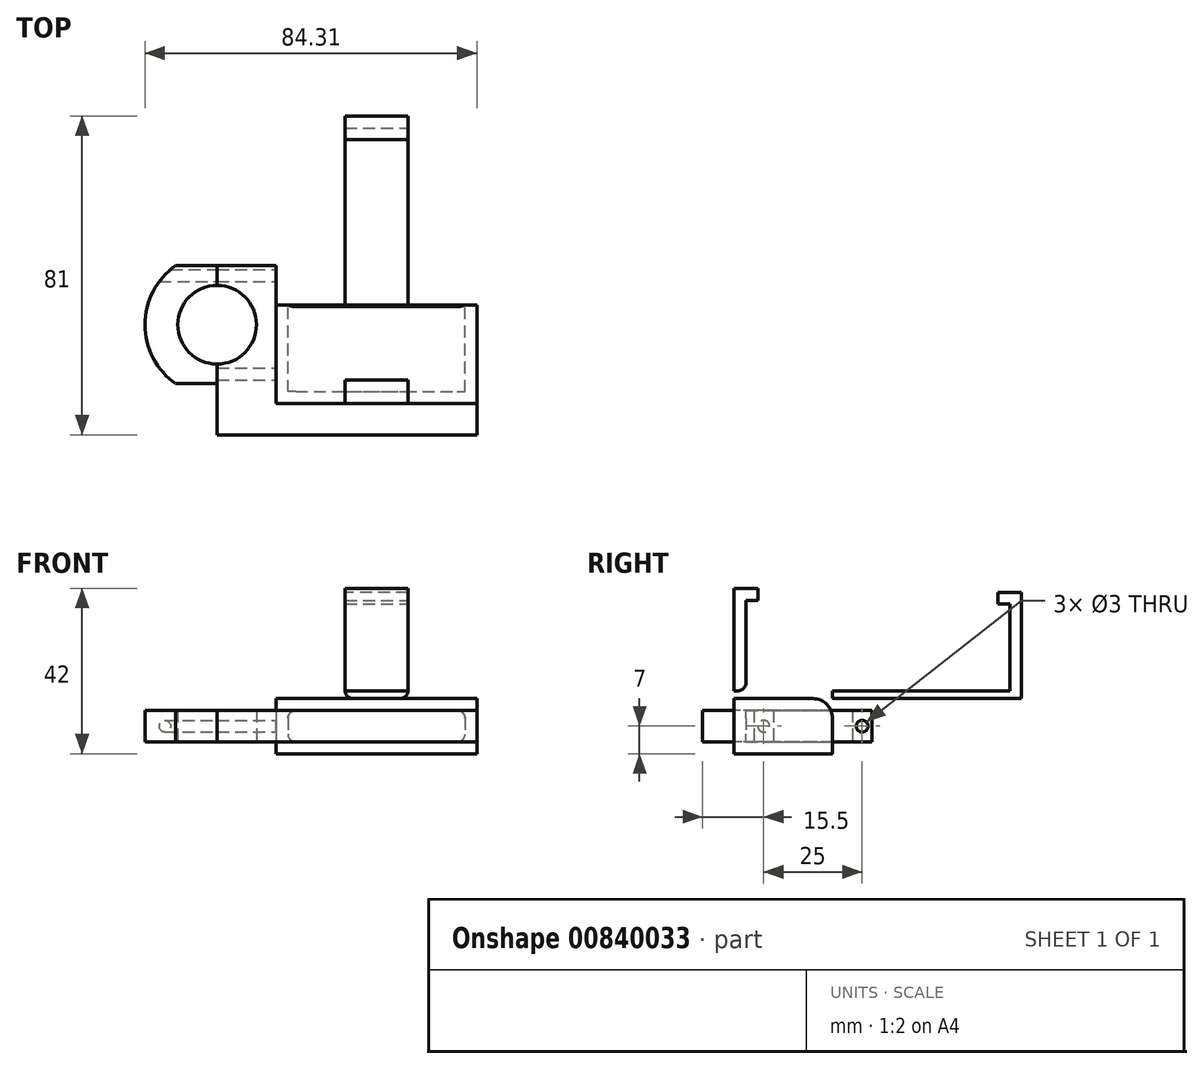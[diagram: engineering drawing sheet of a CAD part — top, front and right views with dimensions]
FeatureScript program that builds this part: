
annotation { "Feature Type Name" : "Feature", "Feature Type Description" : "" }
export const myFeature = defineFeature(function(context is Context, id is Id, definition is map)
    precondition{}
    {
        {
            var Q0;
            Q0=qCreatedBy(makeId("Top.planeOp"),FACE);
            var sketch = newSketch(context, id + "F0", { "sketchPlane" : qUnion([Q0])});
            skArc(sketch, "E0", {"start": v(0, 10) * mm, "mid": v(-10, 0) * mm, "end": v(0, -10) * mm});
            skLineSegment(sketch, "E1.bottom", {"start": v(0, 10) * mm, "end": v(-10.5, 10) * mm});
            skLineSegment(sketch, "E1.top", {"start": v(0, 15) * mm, "end": v(-10.5, 15) * mm});
            skLineSegment(sketch, "E1.left", {"start": v(0, 10) * mm, "end": v(0, 15) * mm});
            skLineSegment(sketch, "E1.right", {"start": v(-10.5, 10) * mm, "end": v(-10.5, 15) * mm});
            skLineSegment(sketch, "E2.MirrorCS", {"start": v(0, -10) * mm, "end": v(-10.5, -10) * mm});
            skLineSegment(sketch, "E3.MirrorCS", {"start": v(-10.5, -10) * mm, "end": v(-10.5, -15) * mm});
            skLineSegment(sketch, "E4.MirrorCS", {"start": v(0, -15) * mm, "end": v(-10.5, -15) * mm});
            skLineSegment(sketch, "E5.MirrorCS", {"start": v(0, -10) * mm, "end": v(0, -15) * mm});
            skArc(sketch, "E6", {"start": v(-10.5, 15) * mm, "mid": v(-18.3, 0) * mm, "end": v(-10.5, -15) * mm});
            skSolve(sketch);
        }
        {
            var Q0;
            Q0=makeQuery(id+"F0.imprint","IMPRINT",FACE,{"disambiguationData":[TD([[makeQuery(id+"F0.imprint","IMPRINT",EDGE,{"derivedFrom":sQuery(id+"F0.wireOp",EDGE,"E1.bottom")}),-1.0]])]});
            var Q1;
            Q1=makeQuery(id+"F0.imprint","IMPRINT",FACE,{"disambiguationData":[TD([[makeQuery(id+"F0.imprint","IMPRINT",EDGE,{"derivedFrom":sQuery(id+"F0.wireOp",EDGE,"E0")}),-1.0]])]});
            var Q2;
            Q2=makeQuery(id+"F0.imprint","IMPRINT",FACE,{"disambiguationData":[TD([[makeQuery(id+"F0.imprint","IMPRINT",EDGE,{"derivedFrom":sQuery(id+"F0.wireOp",EDGE,"E2.MirrorCS")}),1.0]])]});
            extrude(context, id + "F1", {"entities" : qUnion([Q0, Q1, Q2]), "depth" : 8 * mm, "offsetDistance" : 25 * mm});
        }
        {
            var Q0;
            Q0=makeQuery(id+"F1.opExtrude","SWEPT_FACE",FACE,{"disambiguationData":[OSD([sQuery(id+"F0.wireOp",EDGE,"E1.left")])]});
            var sketch = newSketch(context, id + "F2", { "sketchPlane" : qUnion([Q0])});
            skCircle(sketch, "E7", {"center": v(12.5, 4) * mm, "radius": 1.5 * mm});
            skPoint(sketch, "E7.centerSnap0", {"position": v(10, 4) * mm});
            skPoint(sketch, "E7.centerSnap1", {"position": v(12.5, 8) * mm});
            skCircle(sketch, "E8.MirrorC", {"center": v(-12.5, 4) * mm, "radius": 1.5 * mm});
            skSolve(sketch);
        }
        {
            var Q0;
            Q0=makeQuery(id+"F2.imprint","IMPRINT",FACE,{"disambiguationData":[TD([[makeQuery(id+"F2.imprint","IMPRINT",EDGE,{"derivedFrom":sQuery(id+"F2.wireOp",EDGE,"E7")}),1.0]])]});
            var Q1;
            Q1=makeQuery(id+"F2.imprint","IMPRINT",FACE,{"disambiguationData":[TD([[makeQuery(id+"F2.imprint","IMPRINT",EDGE,{"derivedFrom":sQuery(id+"F2.wireOp",EDGE,"E8.MirrorC")}),-1.0]])]});
            extrude(context, id + "F3", {"entities" : qUnion([Q0, Q1]), "operationType" : NewBodyOperationType.REMOVE, "endBound" : BoundingType.UP_TO_NEXT, "oppositeDirection" : true, "depth" : 25 * mm, "offsetDistance" : 25 * mm});
        }
        {
            var Q0;
            Q0=qCreatedBy(makeId("Top.planeOp"),FACE);
            var sketch = newSketch(context, id + "F4", { "sketchPlane" : qUnion([Q0])});
            skLineSegment(sketch, "E9.0", {"start": v(0, 15) * mm, "end": v(-10.5, 15) * mm});
            skLineSegment(sketch, "E9.1", {"start": v(0, 10) * mm, "end": v(0, 15) * mm});
            skArc(sketch, "E9.2", {"start": v(0, 10) * mm, "mid": v(-10, 0) * mm, "end": v(0, -10) * mm});
            skLineSegment(sketch, "E9.3", {"start": v(0, -10) * mm, "end": v(0, -15) * mm});
            skLineSegment(sketch, "E9.4", {"start": v(0, -15) * mm, "end": v(-10.5, -15) * mm});
            skArc(sketch, "E9.5", {"start": v(-10.5, 15) * mm, "mid": v(-18.3, 0) * mm, "end": v(-10.5, -15) * mm});
            skArc(sketch, "E10", {"start": v(0, -10) * mm, "mid": v(10, 0) * mm, "end": v(0, 10) * mm});
            skLineSegment(sketch, "E11.bottom", {"start": v(0, 10) * mm, "end": v(15, 10) * mm});
            skLineSegment(sketch, "E11.top", {"start": v(0, 15) * mm, "end": v(15, 15) * mm});
            skLineSegment(sketch, "E11.right", {"start": v(15, 10) * mm, "end": v(15, 15) * mm});
            skLineSegment(sketch, "E12.MirrorCS", {"start": v(0, -10) * mm, "end": v(15, -10) * mm});
            skLineSegment(sketch, "E13.MirrorCS", {"start": v(15, -10) * mm, "end": v(15, -15) * mm});
            skLineSegment(sketch, "E14.MirrorCS", {"start": v(0, -15) * mm, "end": v(15, -15) * mm});
            skLineSegment(sketch, "E15", {"start": v(15, 10) * mm, "end": v(15, -10) * mm});
            skLineSegment(sketch, "E16.top", {"start": v(0, -20) * mm, "end": v(15, -20) * mm});
            skLineSegment(sketch, "E16.left", {"start": v(0, -15) * mm, "end": v(0, -20) * mm});
            skLineSegment(sketch, "E16.right", {"start": v(15, -15) * mm, "end": v(15, -20) * mm});
            skLineSegment(sketch, "E17.bottom", {"start": v(0, -20) * mm, "end": v(66, -20) * mm});
            skLineSegment(sketch, "E17.top", {"start": v(0, -28) * mm, "end": v(66, -28) * mm});
            skLineSegment(sketch, "E17.left", {"start": v(0, -20) * mm, "end": v(0, -28) * mm});
            skLineSegment(sketch, "E17.right", {"start": v(66, -20) * mm, "end": v(66, -28) * mm});
            skSolve(sketch);
        }
        {
            var Q0;
            Q0=makeQuery(id+"F4.imprint","IMPRINT",FACE,{"disambiguationData":[TD([[makeQuery(id+"F4.imprint","IMPRINT",EDGE,{"derivedFrom":sQuery(id+"F4.wireOp",EDGE,"E10")}),-1.0]])]});
            var Q1;
            Q1=makeQuery(id+"F4.imprint","IMPRINT",FACE,{"disambiguationData":[TD([[makeQuery(id+"F4.imprint","IMPRINT",EDGE,{"derivedFrom":sQuery(id+"F4.wireOp",EDGE,"E9.1")}),-1.0]])]});
            var Q2;
            Q2=makeQuery(id+"F4.imprint","IMPRINT",FACE,{"disambiguationData":[TD([[makeQuery(id+"F4.imprint","IMPRINT",EDGE,{"derivedFrom":sQuery(id+"F4.wireOp",EDGE,"E9.3")}),1.0]])]});
            var Q3;
            Q3=makeQuery(id+"F4.imprint","IMPRINT",FACE,{"disambiguationData":[TD([[makeQuery(id+"F4.imprint","IMPRINT",EDGE,{"derivedFrom":sQuery(id+"F4.wireOp",EDGE,"QlJfyb3Y-pkJ5-ScCR-3cII-RCXO0TggYRWT.top")}),1.0]])]});
            var Q4;
            Q4=makeQuery(id+"F4.imprint","IMPRINT",FACE,{"disambiguationData":[TD([[makeQuery(id+"F4.imprint","IMPRINT",EDGE,{"derivedFrom":sQuery(id+"F4.wireOp",EDGE,"E14.MirrorCS")}),-1.0]])]});
            var Q5;
            Q5=makeQuery(id+"F4.imprint","IMPRINT",FACE,{"disambiguationData":[TD([[makeQuery(id+"F4.imprint","IMPRINT",EDGE,{"derivedFrom":sQuery(id+"F4.wireOp",EDGE,"E16.top")}),-1.0]])]});
            extrude(context, id + "F5", {"entities" : qUnion([Q0, Q1, Q2, Q3, Q4, Q5]), "depth" : 8 * mm, "offsetDistance" : 25 * mm});
        }
        {
            var Q0;
            Q0=makeQuery(id+"F5.opExtrude","SWEPT_FACE",FACE,{"disambiguationData":[OSD([sQuery(id+"F4.wireOp",EDGE,"E11.right"),sQuery(id+"F4.wireOp",EDGE,"E13.MirrorCS"),sQuery(id+"F4.wireOp",EDGE,"E15"),sQuery(id+"F4.wireOp",EDGE,"E16.right")])]});
            var sketch = newSketch(context, id + "F6", { "sketchPlane" : qUnion([Q0])});
            skCircle(sketch, "E18.0", {"center": v(12.5, 4) * mm, "radius": 1.5 * mm});
            skCircle(sketch, "E18.1", {"center": v(-12.5, 4) * mm, "radius": 1.5 * mm});
            skSolve(sketch);
        }
        {
            var Q0;
            Q0=makeQuery(id+"F6.imprint","IMPRINT",FACE,{"disambiguationData":[TD([[makeQuery(id+"F6.imprint","IMPRINT",EDGE,{"derivedFrom":sQuery(id+"F6.wireOp",EDGE,"E18.1")}),1.0]])]});
            var Q1;
            Q1=makeQuery(id+"F6.imprint","IMPRINT",FACE,{"disambiguationData":[TD([[makeQuery(id+"F6.imprint","IMPRINT",EDGE,{"derivedFrom":sQuery(id+"F6.wireOp",EDGE,"E18.0")}),1.0]])]});
            extrude(context, id + "F7", {"entities" : qUnion([Q0, Q1]), "operationType" : NewBodyOperationType.REMOVE, "endBound" : BoundingType.UP_TO_NEXT, "oppositeDirection" : true, "depth" : 25 * mm, "offsetDistance" : 25 * mm});
        }
        {
            var Q0;
            Q0=makeQuery(id+"F5.opExtrude","SWEPT_FACE",FACE,{"disambiguationData":[OSD([sQuery(id+"F4.wireOp",EDGE,"E17.bottom")])]});
            var sketch = newSketch(context, id + "F8", { "sketchPlane" : qUnion([Q0])});
            skLineSegment(sketch, "E19.bottom", {"start": v(-15, 11) * mm, "end": v(-66, 11) * mm});
            skLineSegment(sketch, "E19.top", {"start": v(-15, -3) * mm, "end": v(-66, -3) * mm});
            skLineSegment(sketch, "E19.left", {"start": v(-15, 11) * mm, "end": v(-15, -3) * mm});
            skLineSegment(sketch, "E19.right", {"start": v(-66, 11) * mm, "end": v(-66, -3) * mm});
            skSolve(sketch);
        }
        {
            var Q0;
            {var subQ0=sQuery(id+"F8.wireOp",EDGE,"E19.bottom");Q0=makeQuery(id+"F8.imprint","IMPRINT",FACE,{"disambiguationData":[TD([[makeQuery(id+"F8.imprint","IMPRINT",EDGE,{"derivedFrom":subQ0}),1.0]])]});}
            var Q1;
            {var subQ1=sQuery(id+"F4.wireOp",EDGE,"E17.bottom");var subQ2=makeQuery(id+"F5.opExtrude","CAP_EDGE",EDGE,{"disambiguationData":[OSD([subQ1])],"isStart":true});Q1=makeQuery(id+"F8.imprint","IMPRINT",FACE,{"disambiguationData":[TD([[makeQuery(id+"F8.imprint","IMPRINT",EDGE,{"derivedFrom":subQ2}),-1.0]])]});}
            var Q2;
            {var subQ0=sQuery(id+"F8.wireOp",EDGE,"E19.top");Q2=makeQuery(id+"F8.imprint","IMPRINT",FACE,{"disambiguationData":[TD([[makeQuery(id+"F8.imprint","IMPRINT",EDGE,{"derivedFrom":subQ0}),-1.0]])]});}
            extrude(context, id + "F9", {"entities" : qUnion([Q0, Q1, Q2]), "depth" : 25 * mm, "offsetDistance" : 25 * mm});
        }
        {
            var Q0;
            Q0=makeQuery(id+"F9.opExtrude","CAP_FACE",FACE,{"disambiguationData":[OSD([sQuery(id+"F8.wireOp",EDGE,"E19.bottom"),sQuery(id+"F8.wireOp",EDGE,"E19.top"),sQuery(id+"F8.wireOp",EDGE,"E19.left"),sQuery(id+"F8.wireOp",EDGE,"E19.right")])],"isStart":false});
            var sketch = newSketch(context, id + "F10", { "sketchPlane" : qUnion([Q0])});
            skLineSegment(sketch, "E20.0", {"start": v(-18, 6) * mm, "end": v(-18, 2) * mm});
            skLineSegment(sketch, "E20.1", {"start": v(-20, 8) * mm, "end": v(-61, 8) * mm});
            skLineSegment(sketch, "E20.2", {"start": v(-63, 6) * mm, "end": v(-63, 2) * mm});
            skLineSegment(sketch, "E20.3", {"start": v(-20, 0) * mm, "end": v(-61, 0) * mm});
            skPoint(sketch, "E21.visualSharp", {"position": v(-18, 8) * mm});
            skArc(sketch, "E21.filletArc", {"start": v(-18, 6) * mm, "mid": v(-18.59, 7.41) * mm, "end": v(-20, 8) * mm});
            skPoint(sketch, "E22.visualSharp", {"position": v(-18, 0) * mm});
            skArc(sketch, "E22.filletArc", {"start": v(-20, 0) * mm, "mid": v(-18.59, 0.59) * mm, "end": v(-18, 2) * mm});
            skPoint(sketch, "E23.visualSharp", {"position": v(-63, 0) * mm});
            skArc(sketch, "E23.filletArc", {"start": v(-63, 2) * mm, "mid": v(-62.41, 0.59) * mm, "end": v(-61, 0) * mm});
            skPoint(sketch, "E24.visualSharp", {"position": v(-63, 8) * mm});
            skArc(sketch, "E24.filletArc", {"start": v(-61, 8) * mm, "mid": v(-62.41, 7.41) * mm, "end": v(-63, 6) * mm});
            skSolve(sketch);
        }
        {
            var Q0;
            Q0=makeQuery(id+"F10.imprint","IMPRINT",FACE,{"disambiguationData":[TD([[makeQuery(id+"F10.imprint","IMPRINT",EDGE,{"derivedFrom":sQuery(id+"F10.wireOp",EDGE,"E20.0")}),-1.0]])]});
            extrude(context, id + "F11", {"entities" : qUnion([Q0]), "operationType" : NewBodyOperationType.REMOVE, "oppositeDirection" : true, "depth" : 22 * mm, "offsetDistance" : 25 * mm});
        }
        {
            var Q0;
            Q0=makeQuery(id+"F9.opExtrude","SWEPT_FACE",FACE,{"disambiguationData":[OSD([sQuery(id+"F8.wireOp",EDGE,"E19.bottom")])]});
            var sketch = newSketch(context, id + "F12", { "sketchPlane" : qUnion([Q0])});
            skLineSegment(sketch, "E25.0", {"start": v(66, 5) * mm, "end": v(66, -20) * mm});
            skLineSegment(sketch, "E25.1", {"start": v(15, 5) * mm, "end": v(66, 5) * mm});
            skLineSegment(sketch, "E25.2", {"start": v(15, -20) * mm, "end": v(66, -20) * mm});
            skLineSegment(sketch, "E25.3", {"start": v(15, 5) * mm, "end": v(15, -20) * mm});
            skLineSegment(sketch, "E26.bottom", {"start": v(48.5, -20) * mm, "end": v(32.5, -20) * mm});
            skLineSegment(sketch, "E26.top", {"start": v(48.5, 53) * mm, "end": v(32.5, 53) * mm});
            skLineSegment(sketch, "E26.left", {"start": v(48.5, -20) * mm, "end": v(48.5, 53) * mm});
            skLineSegment(sketch, "E26.right", {"start": v(32.5, -20) * mm, "end": v(32.5, 53) * mm});
            skPoint(sketch, "E27", {"position": v(40.5, -20) * mm});
            skSolve(sketch);
        }
        {
            var Q0;
            {var subQ5=sQuery(id+"F12.wireOp",EDGE,"E26.top");Q0=makeQuery(id+"F12.imprint","IMPRINT",FACE,{"disambiguationData":[TD([[makeQuery(id+"F12.imprint","IMPRINT",EDGE,{"derivedFrom":subQ5}),1.0]])]});}
            var Q1;
            {var subQ5=sQuery(id+"F12.wireOp",EDGE,"E26.bottom");Q1=makeQuery(id+"F12.imprint","IMPRINT",FACE,{"disambiguationData":[TD([[makeQuery(id+"F12.imprint","IMPRINT",EDGE,{"derivedFrom":subQ5}),1.0]])]});}
            extrude(context, id + "F13", {"entities" : qUnion([Q0, Q1]), "operationType" : NewBodyOperationType.ADD, "depth" : 2 * mm, "offsetDistance" : 25 * mm});
        }
        {
            var Q0;
            Q0=makeQuery(id+"F13.opExtrude","CAP_FACE",FACE,{"disambiguationData":[OSD([sQuery(id+"F12.wireOp",EDGE,"E26.bottom"),sQuery(id+"F12.wireOp",EDGE,"E26.top"),sQuery(id+"F12.wireOp",EDGE,"E26.left"),sQuery(id+"F12.wireOp",EDGE,"E26.right")])],"isStart":false});
            var sketch = newSketch(context, id + "F14", { "sketchPlane" : qUnion([Q0])});
            skLineSegment(sketch, "E28.bottom", {"start": v(48.5, -20) * mm, "end": v(32.5, -20) * mm});
            skLineSegment(sketch, "E28.top", {"start": v(48.5, -17) * mm, "end": v(32.5, -17) * mm});
            skLineSegment(sketch, "E28.left", {"start": v(48.5, -20) * mm, "end": v(48.5, -17) * mm});
            skLineSegment(sketch, "E28.right", {"start": v(32.5, -20) * mm, "end": v(32.5, -17) * mm});
            skLineSegment(sketch, "E29.bottom", {"start": v(32.5, 53) * mm, "end": v(48.5, 53) * mm});
            skLineSegment(sketch, "E29.top", {"start": v(32.5, 50) * mm, "end": v(48.5, 50) * mm});
            skLineSegment(sketch, "E29.left", {"start": v(32.5, 53) * mm, "end": v(32.5, 50) * mm});
            skLineSegment(sketch, "E29.right", {"start": v(48.5, 53) * mm, "end": v(48.5, 50) * mm});
            skSolve(sketch);
        }
        {
            var Q0;
            Q0=makeQuery(id+"F14.imprint","IMPRINT",FACE,{"disambiguationData":[TD([[makeQuery(id+"F14.imprint","IMPRINT",EDGE,{"derivedFrom":sQuery(id+"F14.wireOp",EDGE,"E29.bottom")}),1.0]])]});
            extrude(context, id + "F15", {"entities" : qUnion([Q0]), "operationType" : NewBodyOperationType.ADD, "depth" : 22 * mm, "offsetDistance" : 25 * mm});
        }
        {
            var Q0;
            Q0=makeQuery(id+"F15.opExtrude","CAP_FACE",FACE,{"disambiguationData":[OSD([sQuery(id+"F14.wireOp",EDGE,"E29.bottom"),sQuery(id+"F14.wireOp",EDGE,"E29.top"),sQuery(id+"F14.wireOp",EDGE,"E29.left"),sQuery(id+"F14.wireOp",EDGE,"E29.right")])],"isStart":false});
            var sketch = newSketch(context, id + "F16", { "sketchPlane" : qUnion([Q0])});
            skLineSegment(sketch, "E30.bottom", {"start": v(32.5, 53) * mm, "end": v(48.5, 53) * mm});
            skLineSegment(sketch, "E30.top", {"start": v(32.5, 47) * mm, "end": v(48.5, 47) * mm});
            skLineSegment(sketch, "E30.left", {"start": v(32.5, 53) * mm, "end": v(32.5, 47) * mm});
            skLineSegment(sketch, "E30.right", {"start": v(48.5, 53) * mm, "end": v(48.5, 47) * mm});
            skSolve(sketch);
        }
        {
            var Q0;
            {var subQ0=sQuery(id+"F16.wireOp",EDGE,"E30.top");Q0=makeQuery(id+"F16.imprint","IMPRINT",FACE,{"disambiguationData":[TD([[makeQuery(id+"F16.imprint","IMPRINT",EDGE,{"derivedFrom":subQ0}),1.0]])]});}
            var Q1;
            {var subQ0=sQuery(id+"F16.wireOp",EDGE,"E30.bottom");Q1=makeQuery(id+"F16.imprint","IMPRINT",FACE,{"disambiguationData":[TD([[makeQuery(id+"F16.imprint","IMPRINT",EDGE,{"derivedFrom":subQ0}),1.0]])]});}
            extrude(context, id + "F17", {"entities" : qUnion([Q0, Q1]), "operationType" : NewBodyOperationType.ADD, "depth" : 3 * mm, "offsetDistance" : 25 * mm});
        }
        {
            var Q0;
            Q0=makeQuery(id+"F13.opExtrude","CAP_FACE",FACE,{"disambiguationData":[OSD([sQuery(id+"F12.wireOp",EDGE,"E26.bottom"),sQuery(id+"F12.wireOp",EDGE,"E26.top"),sQuery(id+"F12.wireOp",EDGE,"E26.left"),sQuery(id+"F12.wireOp",EDGE,"E26.right")])],"isStart":false});
            var sketch = newSketch(context, id + "F18", { "sketchPlane" : qUnion([Q0])});
            skLineSegment(sketch, "E31.bottom", {"start": v(32.5, -20) * mm, "end": v(48.5, -20) * mm});
            skLineSegment(sketch, "E31.top", {"start": v(32.5, -17) * mm, "end": v(48.5, -17) * mm});
            skLineSegment(sketch, "E31.left", {"start": v(32.5, -20) * mm, "end": v(32.5, -17) * mm});
            skLineSegment(sketch, "E31.right", {"start": v(48.5, -20) * mm, "end": v(48.5, -17) * mm});
            skSolve(sketch);
        }
        {
            var Q0;
            Q0=makeQuery(id+"F18.imprint","IMPRINT",FACE,{"disambiguationData":[TD([[makeQuery(id+"F18.imprint","IMPRINT",EDGE,{"derivedFrom":sQuery(id+"F18.wireOp",EDGE,"E31.bottom")}),1.0]])]});
            extrude(context, id + "F19", {"entities" : qUnion([Q0]), "operationType" : NewBodyOperationType.ADD, "depth" : 23 * mm, "offsetDistance" : 25 * mm});
        }
        {
            var Q0;
            Q0=makeQuery(id+"F19.opExtrude","CAP_FACE",FACE,{"disambiguationData":[OSD([sQuery(id+"F18.wireOp",EDGE,"E31.bottom"),sQuery(id+"F18.wireOp",EDGE,"E31.top"),sQuery(id+"F18.wireOp",EDGE,"E31.left"),sQuery(id+"F18.wireOp",EDGE,"E31.right")])],"isStart":false});
            var sketch = newSketch(context, id + "F20", { "sketchPlane" : qUnion([Q0])});
            skLineSegment(sketch, "E32.bottom", {"start": v(32.5, -20) * mm, "end": v(48.5, -20) * mm});
            skLineSegment(sketch, "E32.top", {"start": v(32.5, -14) * mm, "end": v(48.5, -14) * mm});
            skLineSegment(sketch, "E32.left", {"start": v(32.5, -20) * mm, "end": v(32.5, -14) * mm});
            skLineSegment(sketch, "E32.right", {"start": v(48.5, -20) * mm, "end": v(48.5, -14) * mm});
            skSolve(sketch);
        }
        {
            var Q0;
            {var subQ0=sQuery(id+"F20.wireOp",EDGE,"E32.top");Q0=makeQuery(id+"F20.imprint","IMPRINT",FACE,{"disambiguationData":[TD([[makeQuery(id+"F20.imprint","IMPRINT",EDGE,{"derivedFrom":subQ0}),-1.0]])]});}
            var Q1;
            {var subQ0=sQuery(id+"F20.wireOp",EDGE,"E32.bottom");Q1=makeQuery(id+"F20.imprint","IMPRINT",FACE,{"disambiguationData":[TD([[makeQuery(id+"F20.imprint","IMPRINT",EDGE,{"derivedFrom":subQ0}),1.0]])]});}
            extrude(context, id + "F21", {"entities" : qUnion([Q0, Q1]), "operationType" : NewBodyOperationType.ADD, "depth" : 3 * mm, "offsetDistance" : 25 * mm});
        }
        {
            var Q0;
            {var subQ0=sQuery(id+"F12.wireOp",EDGE,"E26.right");Q0=makeQuery(id+"F13.boolean.opBoolean","SPLIT",EDGE,{"disambiguationData":[topologyDisambiguationEdgeConnected([makeQuery(id+"F9.opExtrude","SWEPT_FACE",FACE,{"disambiguationData":[OSD([sQuery(id+"F8.wireOp",EDGE,"E19.bottom")])]})])],"derivedFrom":makeQuery(id+"F13.opExtrude","CAP_EDGE",EDGE,{"disambiguationData":[OSD([subQ0])],"isStart":true})});}
            var Q1;
            {var subQ0=sQuery(id+"F12.wireOp",EDGE,"E26.left");Q1=makeQuery(id+"F13.boolean.opBoolean","SPLIT",EDGE,{"disambiguationData":[topologyDisambiguationEdgeConnected([makeQuery(id+"F9.opExtrude","SWEPT_FACE",FACE,{"disambiguationData":[OSD([sQuery(id+"F8.wireOp",EDGE,"E19.bottom")])]})])],"derivedFrom":makeQuery(id+"F13.opExtrude","CAP_EDGE",EDGE,{"disambiguationData":[OSD([subQ0])],"isStart":true})});}
            fillet(context, id + "F22", {"entities" : qUnion([Q0, Q1]), "radius" : 2 * mm, "tangentPropagation" : true, "allowEdgeOverflow" : false});
        }
        {
            var Q0;
            Q0=makeQuery(id+"F19.opExtrude","CAP_EDGE",EDGE,{"disambiguationData":[OSD([sQuery(id+"F18.wireOp",EDGE,"E31.top")])],"isStart":true});
            var Q1;
            Q1=makeQuery(id+"F19.opExtrude","CAP_EDGE",EDGE,{"disambiguationData":[OSD([sQuery(id+"F18.wireOp",EDGE,"E31.top")])],"isStart":false});
            var Q2;
            Q2=makeQuery(id+"F15.opExtrude","CAP_EDGE",EDGE,{"disambiguationData":[OSD([sQuery(id+"F14.wireOp",EDGE,"E29.top")])],"isStart":true});
            var Q3;
            Q3=makeQuery(id+"F15.opExtrude","CAP_EDGE",EDGE,{"disambiguationData":[OSD([sQuery(id+"F14.wireOp",EDGE,"E29.top")])],"isStart":false});
            fillet(context, id + "F23", {"entities" : qUnion([Q0, Q1, Q2, Q3]), "radius" : 2 * mm, "tangentPropagation" : true, "allowEdgeOverflow" : false});
        }
        {
            var Q0;
            {var subQ0=sQuery(id+"F8.wireOp",EDGE,"E19.bottom");Q0=makeQuery(id+"F13.boolean.opBoolean","SPLIT",EDGE,{"disambiguationData":[topologyDisambiguationEdgeConnected([makeQuery(id+"F9.opExtrude","CAP_FACE",FACE,{"disambiguationData":[OSD([subQ0,sQuery(id+"F8.wireOp",EDGE,"E19.top"),sQuery(id+"F8.wireOp",EDGE,"E19.left"),sQuery(id+"F8.wireOp",EDGE,"E19.right")])],"isStart":false}),makeQuery(id+"F13.opExtrude","CAP_FACE",FACE,{"disambiguationData":[OSD([sQuery(id+"F12.wireOp",EDGE,"E26.bottom"),sQuery(id+"F12.wireOp",EDGE,"E26.top"),sQuery(id+"F12.wireOp",EDGE,"E26.left"),sQuery(id+"F12.wireOp",EDGE,"E26.right")])],"isStart":true})])],"derivedFrom":makeQuery(id+"F9.opExtrude","CAP_EDGE",EDGE,{"disambiguationData":[OSD([subQ0])],"isStart":false})});}
            fillet(context, id + "F24", {"entities" : qUnion([Q0]), "radius" : 5 * mm, "tangentPropagation" : true, "allowEdgeOverflow" : false});
        }
    });
